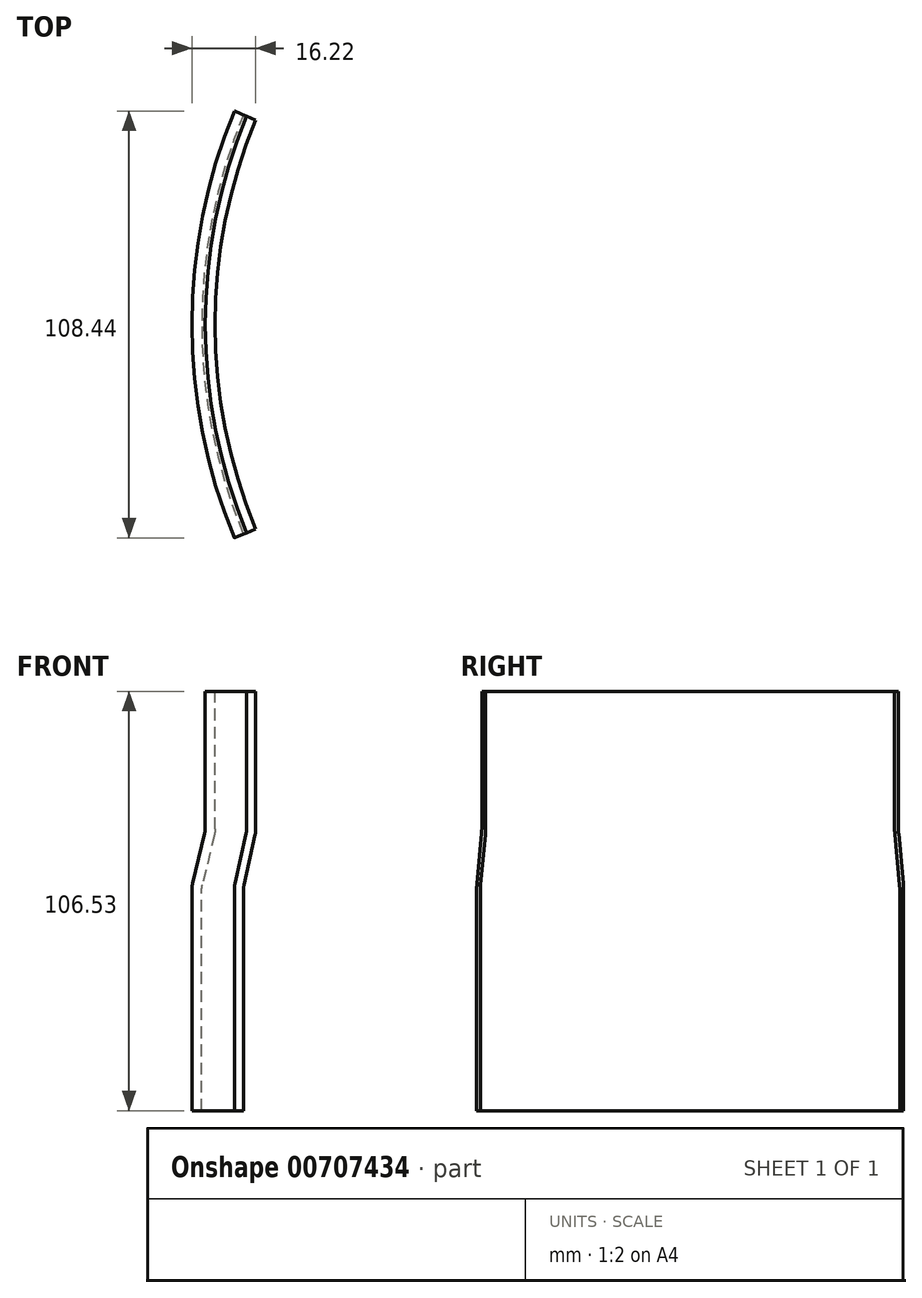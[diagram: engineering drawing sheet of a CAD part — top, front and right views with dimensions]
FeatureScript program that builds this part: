
annotation { "Feature Type Name" : "Feature", "Feature Type Description" : "" }
export const myFeature = defineFeature(function(context is Context, id is Id, definition is map)
    precondition{}
    {
        {
            var Q0;
            Q0=qCreatedBy(makeId("Front.planeOp"),FACE);
            var sketch = newSketch(context, id + "F0", { "sketchPlane" : qUnion([Q0])});
            skLineSegment(sketch, "E0", {"start": v(-138.3, 29.27) * mm, "end": v(-138.3, 63.98) * mm});
            skLineSegment(sketch, "E1", {"start": v(-140.3, 31.45) * mm, "end": v(-140.3, 27.45) * mm});
            skLineSegment(sketch, "E2", {"start": v(-138.46, 27.88) * mm, "end": v(-141.52, 15.12) * mm});
            skLineSegment(sketch, "E3", {"start": v(-141.68, 13.73) * mm, "end": v(-141.68, -42.55) * mm});
            skLineSegment(sketch, "E4.0", {"start": v(-135.8, 28.98) * mm, "end": v(-135.8, 63.98) * mm});
            skLineSegment(sketch, "E4.1", {"start": v(-135.96, 27.58) * mm, "end": v(-139.02, 14.83) * mm});
            skLineSegment(sketch, "E4.2", {"start": v(-139.18, 13.43) * mm, "end": v(-139.18, -42.55) * mm});
            skPoint(sketch, "E5.visualSharp", {"position": v(-141.68, 14.44) * mm});
            skArc(sketch, "E5.filletArc", {"start": v(-141.52, 15.12) * mm, "mid": v(-141.64, 14.43) * mm, "end": v(-141.68, 13.73) * mm});
            skPoint(sketch, "E6.visualSharp", {"position": v(-139.18, 14.14) * mm});
            skArc(sketch, "E6.filletArc", {"start": v(-139.02, 14.83) * mm, "mid": v(-139.14, 14.14) * mm, "end": v(-139.18, 13.43) * mm});
            skPoint(sketch, "E7.visualSharp", {"position": v(-135.8, 28.27) * mm});
            skArc(sketch, "E7.filletArc", {"start": v(-135.96, 27.58) * mm, "mid": v(-135.84, 28.27) * mm, "end": v(-135.8, 28.98) * mm});
            skPoint(sketch, "E8.visualSharp", {"position": v(-138.3, 28.57) * mm});
            skArc(sketch, "E8.filletArc", {"start": v(-138.46, 27.88) * mm, "mid": v(-138.34, 28.57) * mm, "end": v(-138.3, 29.27) * mm});
            skLineSegment(sketch, "E9", {"start": v(-139.18, -42.55) * mm, "end": v(-141.68, -42.55) * mm});
            skLineSegment(sketch, "E10", {"start": v(-135.8, 63.98) * mm, "end": v(-138.3, 63.98) * mm});
            skLineSegment(sketch, "E11", {"start": v(0, 70.75) * mm, "end": v(0, -91.67) * mm, "construction": true});
            skSolve(sketch);
        }
        {
            var Q0;
            Q0=makeQuery(id+"F0.imprint","IMPRINT",FACE,{"disambiguationData":[TD([[makeQuery(id+"F0.imprint","IMPRINT",EDGE,{"derivedFrom":sQuery(id+"F0.wireOp",EDGE,"E0")}),-1.0]])]});
            var Q1;
            Q1=sQuery(id+"F0.wireOp",EDGE,"E11");
            revolve(context, id + "F1", {"surfaceOperationType" : NewSurfaceOperationType.NEW, "entities" : qUnion([Q0]), "axis" : qUnion([Q1]), "revolveType" : RevolveType.SYMMETRIC, "angle" : 45 * degree});
        }
    });
